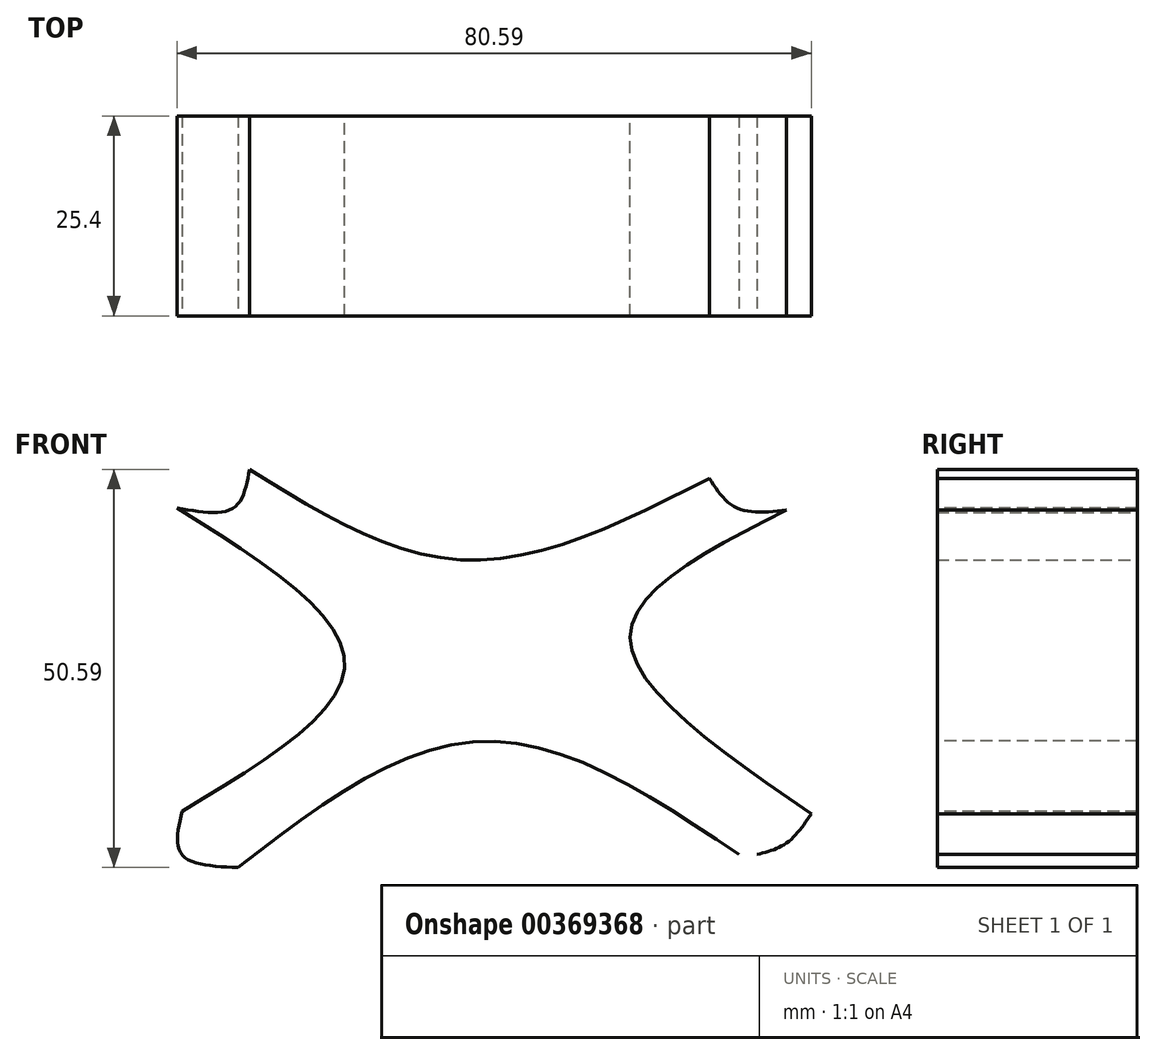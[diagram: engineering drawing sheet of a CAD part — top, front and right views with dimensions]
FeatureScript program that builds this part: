
annotation { "Feature Type Name" : "Feature", "Feature Type Description" : "" }
export const myFeature = defineFeature(function(context is Context, id is Id, definition is map)
    precondition{}
    {
        {
            var Q0;
            Q0=qCreatedBy(makeId("Front.planeOp"),FACE);
            var sketch = newSketch(context, id + "F0", { "sketchPlane" : qUnion([Q0])});
            skFitSpline(sketch, "E0", {"points": [v(-39.38, 17.84) * mm, v(-12.03, 6.33) * mm, v(19.05, 16.7) * mm], "startDerivative": vector(54.96, -34.3) * mm, "endDerivative": vector(61.83, 31.45) * mm});
            skFitSpline(sketch, "E1", {"points": [v(-40.83, -32.75) * mm, v(-9.73, -16.7) * mm, v(22.8, -31.08) * mm], "startDerivative": vector(61.21, 47.66) * mm, "endDerivative": vector(65.36, -43.96) * mm});
            skFitSpline(sketch, "E2", {"points": [v(28.83, 12.66) * mm, v(8.98, -3.17) * mm, v(32, -25.9) * mm], "startDerivative": vector(-62.4, -31.54) * mm, "endDerivative": vector(66.14, -45.31) * mm});
            skFitSpline(sketch, "E3", {"points": [v(-47.96, -25.6) * mm, v(-27.29, -6.9) * mm, v(-48.59, 12.95) * mm], "startDerivative": vector(62.67, 37.44) * mm, "endDerivative": vector(-63.38, 39.68) * mm});
            skFitSpline(sketch, "E4", {"points": [v(-48.59, 12.95) * mm, v(-41.4, 12.95) * mm, v(-39.38, 17.84) * mm], "startDerivative": vector(15.79, -2.85) * mm, "endDerivative": vector(2.29, 13.04) * mm});
            skFitSpline(sketch, "E5", {"points": [v(19.05, 16.7) * mm, v(22.5, 12.95) * mm, v(28.83, 12.66) * mm], "startDerivative": vector(6.2, -9.66) * mm, "endDerivative": vector(13.25, 1.4) * mm});
            skFitSpline(sketch, "E6", {"points": [v(32, -25.9) * mm, v(28.83, -29.64) * mm, v(25.1, -31.08) * mm], "startDerivative": vector(-5.54, -8.2) * mm, "endDerivative": vector(-8.32, -2.06) * mm});
            skFitSpline(sketch, "E7", {"points": [v(-47.96, -25.6) * mm, v(-47.96, -31.08) * mm, v(-40.83, -32.75) * mm], "startDerivative": vector(-3.09, -13.85) * mm, "endDerivative": vector(16.87, -0.78) * mm});
            skSolve(sketch);
        }
        {
            var Q0;
            Q0=sQuery(id+"F0.wireOp",EDGE,"E1");
            var Q1;
            Q1=sQuery(id+"F0.wireOp",EDGE,"E3");
            var Q2;
            Q2=sQuery(id+"F0.wireOp",EDGE,"E0");
            var Q3;
            Q3=sQuery(id+"F0.wireOp",EDGE,"E2");
            var Q4;
            Q4=sQuery(id+"F0.wireOp",EDGE,"E5");
            var Q5;
            Q5=sQuery(id+"F0.wireOp",EDGE,"E7");
            var Q6;
            Q6=sQuery(id+"F0.wireOp",EDGE,"E6");
            var Q7;
            Q7=sQuery(id+"F0.wireOp",EDGE,"E4");
            extrude(context, id + "F1", {"bodyType" : ToolBodyType.SURFACE, "surfaceEntities" : qUnion([Q0, Q1, Q2, Q3, Q4, Q5, Q6, Q7]), "depth" : 25.4 * mm});
        }
    });
